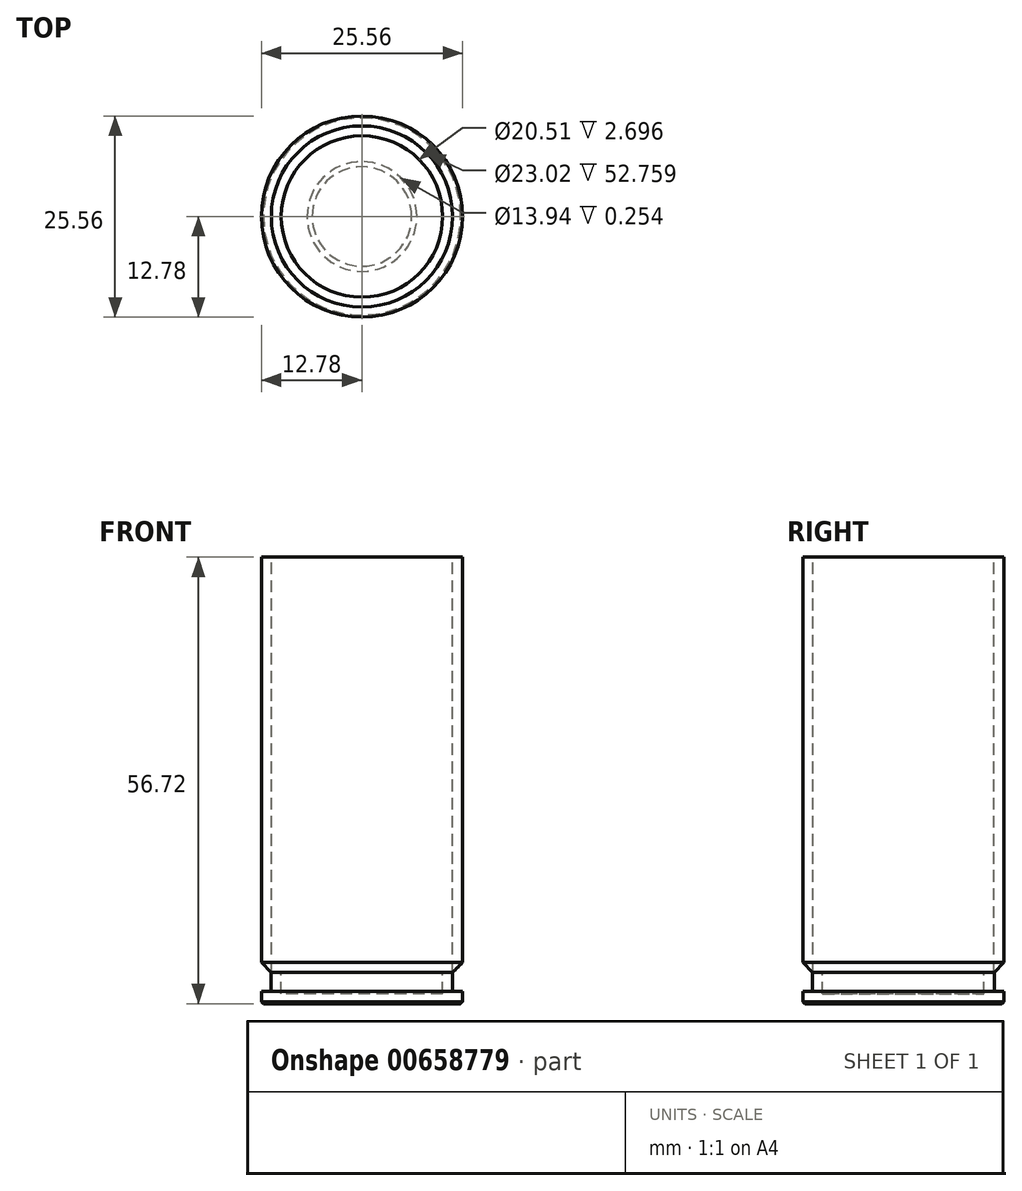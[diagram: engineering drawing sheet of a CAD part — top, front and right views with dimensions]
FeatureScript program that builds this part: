
annotation { "Feature Type Name" : "Feature", "Feature Type Description" : "" }
export const myFeature = defineFeature(function(context is Context, id is Id, definition is map)
    precondition{}
    {
        {
            var Q0;
            Q0=qCreatedBy(makeId("Front.planeOp"),FACE);
            var sketch = newSketch(context, id + "F0", { "sketchPlane" : qUnion([Q0])});
            skLineSegment(sketch, "E0", {"start": v(0, 0) * mm, "end": v(12.78, 0) * mm});
            skLineSegment(sketch, "E1", {"start": v(12.78, 56.72) * mm, "end": v(0, 56.72) * mm});
            skLineSegment(sketch, "E2", {"start": v(0, 56.72) * mm, "end": v(0, 0) * mm});
            skLineSegment(sketch, "E3", {"start": v(0, 67.58) * mm, "end": v(0, -19.26) * mm});
            skLineSegment(sketch, "E4", {"start": v(12.78, 0) * mm, "end": v(12.78, 1.59) * mm});
            skLineSegment(sketch, "E5", {"start": v(12.78, 1.59) * mm, "end": v(11.53, 1.59) * mm});
            skLineSegment(sketch, "E6", {"start": v(11.53, 1.59) * mm, "end": v(11.53, 2.7) * mm});
            skLineSegment(sketch, "E7", {"start": v(11.53, 2.7) * mm, "end": v(12.78, 2.7) * mm});
            skLineSegment(sketch, "E8", {"start": v(12.78, 2.7) * mm, "end": v(12.78, 56.72) * mm});
            skSolve(sketch);
        }
        {
            var Q0;
            Q0 = qSketchRegion(id + "F0", true);
            var Q1;
            Q1=sQuery(id+"F0.wireOp",EDGE,"E3");
            revolve(context, id + "F1", {"entities" : qUnion([Q0]), "axis" : qUnion([Q1]), "revolveType" : RevolveType.FULL});
        }
        {
            var Q0;
            Q0=makeQuery(id+"F1.opRevolve","SWEPT_FACE",FACE,{"disambiguationData":[OSD([sQuery(id+"F0.wireOp",EDGE,"E1")])]});
            shell(context, id + "F2", {"entities" : qUnion([Q0]), "thickness" : 1.27 * mm});
        }
        {
            var Q0;
            Q0=makeQuery(id+"F1.opRevolve","SWEPT_EDGE",EDGE,{"disambiguationData":[OSD([sQuery(id+"F0.wireOp",EDGE,"E0"),sQuery(id+"F0.wireOp",EDGE,"E4")])]});
            chamfer(context, id + "F3", {"entities" : qUnion([Q0]), "width" : 0.25 * mm, "tangentPropagation" : true});
        }
        {
            var Q0;
            Q0=makeQuery(id+"F1.opRevolve","SWEPT_FACE",FACE,{"disambiguationData":[OSD([sQuery(id+"F0.wireOp",EDGE,"E0")])]});
            var sketch = newSketch(context, id + "F4", { "sketchPlane" : qUnion([Q0])});
            skCircle(sketch, "E9", {"center": v(0, 0) * mm, "radius": 6.97 * mm});
            skCircle(sketch, "E10", {"center": v(0, 0) * mm, "radius": 6.32 * mm});
            skSolve(sketch);
        }
        {
            var Q0;
            Q0 = qSketchRegion(id + "F4", true);
            extrude(context, id + "F5", {"entities" : qUnion([Q0]), "operationType" : NewBodyOperationType.REMOVE, "oppositeDirection" : true, "depth" : 0.25 * mm, "offsetDistance" : 25.4 * mm});
        }
        {
            var Q0;
            Q0=makeQuery(id+"F5.boolean.opBoolean","COPY",EDGE,{"derivedFrom":makeQuery(id+"F5.opExtrude","CAP_EDGE",EDGE,{"disambiguationData":[OSD([sQuery(id+"F4.wireOp",EDGE,"E10")])],"isStart":true})});
            var Q1;
            Q1=makeQuery(id+"F5.boolean.opBoolean","COPY",EDGE,{"derivedFrom":makeQuery(id+"F5.opExtrude","CAP_EDGE",EDGE,{"disambiguationData":[OSD([sQuery(id+"F4.wireOp",EDGE,"E9")])],"isStart":true})});
            fillet(context, id + "F6", {"entities" : qUnion([Q0, Q1]), "radius" : 0.76 * mm, "tangentPropagation" : true, "allowEdgeOverflow" : false});
        }
        {
            var Q0;
            Q0=makeQuery(id+"F1.opRevolve","SWEPT_EDGE",EDGE,{"disambiguationData":[OSD([sQuery(id+"F0.wireOp",EDGE,"E7"),sQuery(id+"F0.wireOp",EDGE,"E8")])]});
            chamfer(context, id + "F7", {"entities" : qUnion([Q0]), "width" : 2.54 * mm, "tangentPropagation" : true});
        }
    });
